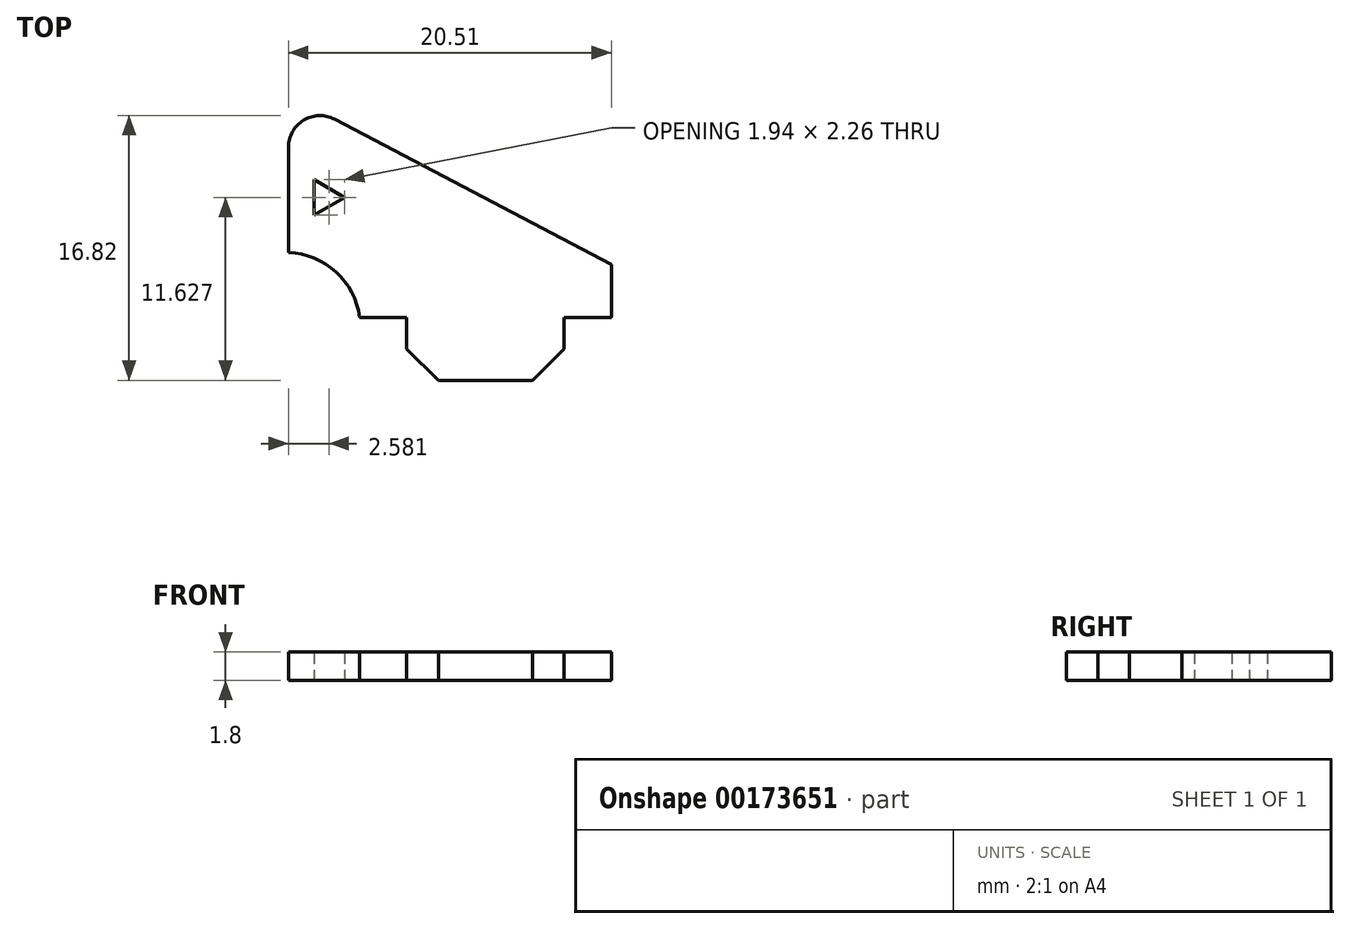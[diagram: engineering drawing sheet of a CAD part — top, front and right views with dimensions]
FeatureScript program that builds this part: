
annotation { "Feature Type Name" : "Feature", "Feature Type Description" : "" }
export const myFeature = defineFeature(function(context is Context, id is Id, definition is map)
    precondition{}
    {
        {
            var Q0;
            Q0=qCreatedBy(makeId("Top.planeOp"),FACE);
            var sketch = newSketch(context, id + "F0", { "sketchPlane" : qUnion([Q0])});
            skLineSegment(sketch, "E0", {"start": v(-14.2, 8.73) * mm, "end": v(-11.2, 8.73) * mm});
            skLineSegment(sketch, "E1", {"start": v(-11.2, 8.73) * mm, "end": v(-11.2, 6.73) * mm});
            skLineSegment(sketch, "E2", {"start": v(-11.2, 6.73) * mm, "end": v(-11.2, 4.73) * mm, "construction": true});
            skLineSegment(sketch, "E3", {"start": v(-11.2, 4.73) * mm, "end": v(-9.2, 4.73) * mm, "construction": true});
            skLineSegment(sketch, "E4", {"start": v(-11.2, 8.73) * mm, "end": v(-1.2, 8.73) * mm, "construction": true});
            skLineSegment(sketch, "E5", {"start": v(-1.2, 8.73) * mm, "end": v(1.8, 8.73) * mm});
            skLineSegment(sketch, "E6", {"start": v(-1.2, 8.73) * mm, "end": v(-1.2, 6.73) * mm});
            skLineSegment(sketch, "E7", {"start": v(-1.2, 6.73) * mm, "end": v(-1.2, 4.73) * mm, "construction": true});
            skLineSegment(sketch, "E8", {"start": v(-1.2, 4.73) * mm, "end": v(-3.2, 4.73) * mm, "construction": true});
            skLineSegment(sketch, "E9", {"start": v(-9.2, 4.73) * mm, "end": v(-3.2, 4.73) * mm});
            skLineSegment(sketch, "E10", {"start": v(-1.2, 6.73) * mm, "end": v(-3.2, 4.73) * mm});
            skLineSegment(sketch, "E11", {"start": v(1.8, 8.73) * mm, "end": v(1.8, 12.07) * mm});
            skCircle(sketch, "E12", {"center": v(-1.2, 8.73) * mm, "radius": 22.5 * mm, "construction": true});
            skCircle(sketch, "E13", {"center": v(-11.2, 8.73) * mm, "radius": 16 * mm, "construction": true});
            skLineSegment(sketch, "E14", {"start": v(1.8, 12.07) * mm, "end": v(-15.79, 21.32) * mm});
            skLineSegment(sketch, "E15", {"start": v(-18.72, 19.55) * mm, "end": v(-18.72, 12.86) * mm, "construction": true});
            skArc(sketch, "E16", {"start": v(-14.2, 8.73) * mm, "mid": v(-15.7, 11.62) * mm, "end": v(-18.72, 12.86) * mm});
            skPoint(sketch, "E17.visualSharp", {"position": v(-18.72, 22.86) * mm});
            skArc(sketch, "E17.filletArc", {"start": v(-15.79, 21.32) * mm, "mid": v(-17.75, 21.26) * mm, "end": v(-18.72, 19.55) * mm});
            skLineSegment(sketch, "E18", {"start": v(-18.72, 19.55) * mm, "end": v(-18.72, 12.86) * mm});
            skCircle(sketch, "E19", {"center": v(-18.72, 12.86) * mm, "radius": 3.5 * mm, "construction": true});
            skLineSegment(sketch, "E20", {"start": v(-18.72, 16.36) * mm, "end": v(-16.47, 16.36) * mm, "construction": true});
            skCircle(sketch, "E21", {"center": v(-16.47, 16.36) * mm, "radius": 1.3 * mm, "construction": true});
            skLineSegment(sketch, "E22", {"start": v(-11.2, 6.73) * mm, "end": v(-9.2, 4.73) * mm});
            skLineSegment(sketch, "E23", {"start": v(-17.1, 17.49) * mm, "end": v(-17.1, 15.23) * mm});
            skLineSegment(sketch, "E24", {"start": v(-17.1, 15.23) * mm, "end": v(-15.17, 16.34) * mm});
            skLineSegment(sketch, "E25", {"start": v(-15.17, 16.34) * mm, "end": v(-17.1, 17.49) * mm});
            skSolve(sketch);
        }
        {
            var Q0;
            Q0=makeQuery(id+"F0.imprint","IMPRINT",FACE,{"disambiguationData":[TD([[makeQuery(id+"F0.imprint","IMPRINT",EDGE,{"derivedFrom":sQuery(id+"F0.wireOp",EDGE,"E0")}),1.0]])]});
            extrude(context, id + "F1", {"entities" : qUnion([Q0]), "depth" : 1.8 * mm});
        }
    });
